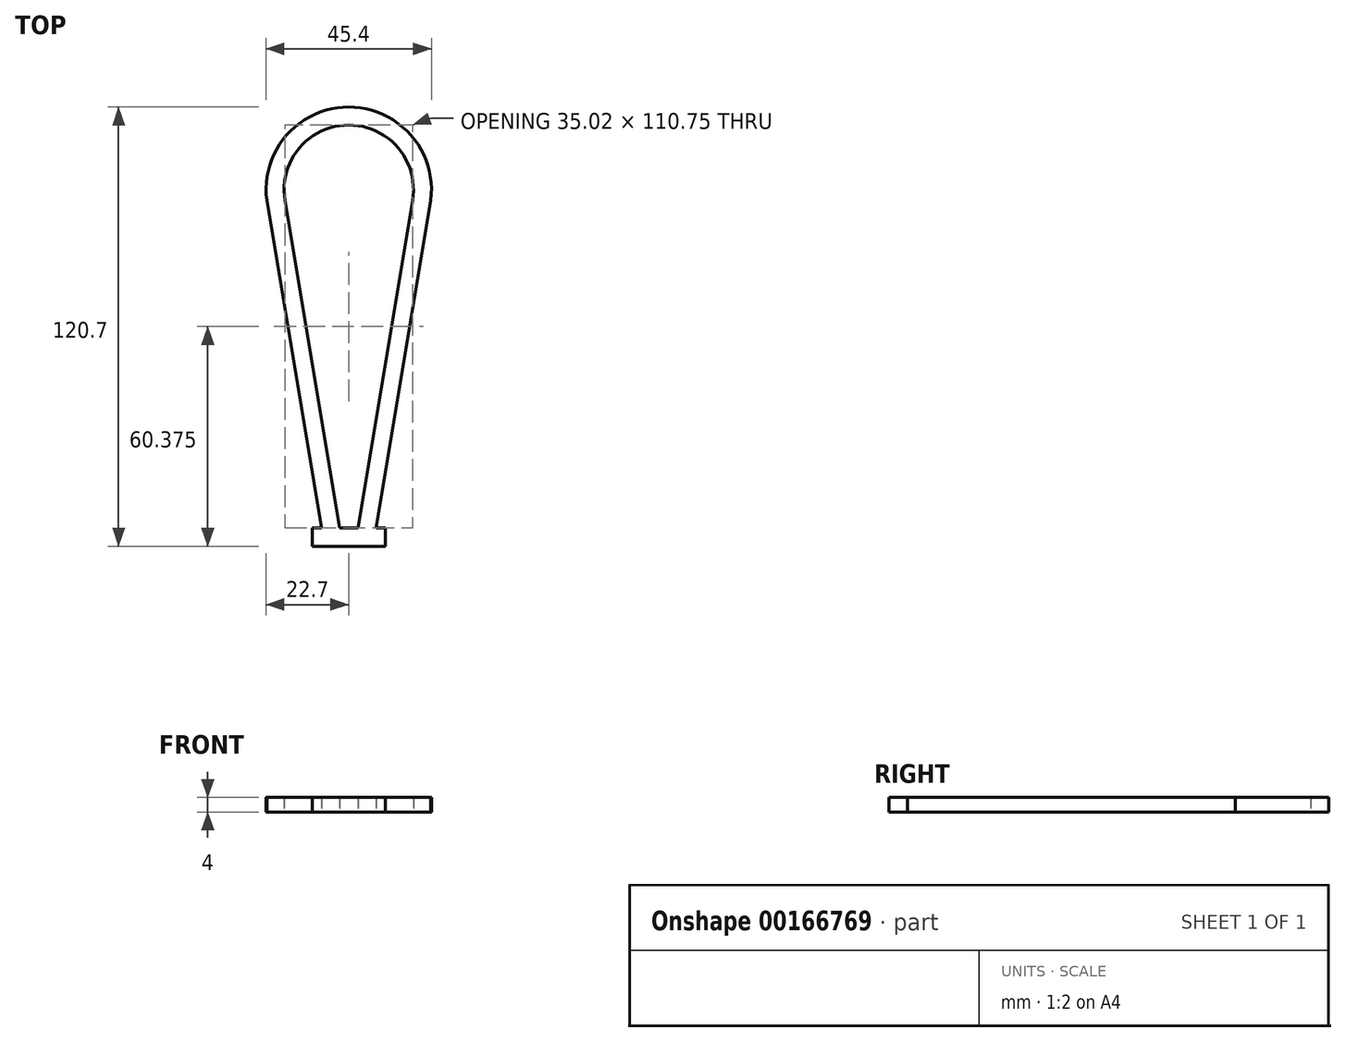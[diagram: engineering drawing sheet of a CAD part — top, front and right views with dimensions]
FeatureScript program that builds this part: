
annotation { "Feature Type Name" : "Feature", "Feature Type Description" : "" }
export const myFeature = defineFeature(function(context is Context, id is Id, definition is map)
    precondition{}
    {
        {
            var Q0;
            Q0=qCreatedBy(makeId("Top.planeOp"),FACE);
            var sketch = newSketch(context, id + "F0", { "sketchPlane" : qUnion([Q0])});
            skPoint(sketch, "E0", {"position": v(0, 108) * mm});
            skArc(sketch, "E1", {"start": v(-17.5, 105.08) * mm, "mid": v(0, 125.75) * mm, "end": v(17.5, 105.08) * mm});
            skLineSegment(sketch, "E2.bottom", {"start": v(10, 15) * mm, "end": v(-10, 15) * mm});
            skLineSegment(sketch, "E2.top", {"start": v(10, 10) * mm, "end": v(-10, 10) * mm});
            skLineSegment(sketch, "E2.left", {"start": v(10, 15) * mm, "end": v(10, 10) * mm});
            skLineSegment(sketch, "E2.right", {"start": v(-10, 15) * mm, "end": v(-10, 10) * mm});
            skPoint(sketch, "E3", {"position": v(-2.5, 15) * mm});
            skPoint(sketch, "E4", {"position": v(2.5, 15) * mm});
            skPoint(sketch, "E4.positionSnap0", {"position": v(0, 15) * mm});
            skLineSegment(sketch, "E5", {"start": v(17.5, 105.08) * mm, "end": v(2.5, 15) * mm});
            skLineSegment(sketch, "E6", {"start": v(-17.5, 105.08) * mm, "end": v(-2.5, 15) * mm});
            skLineSegment(sketch, "E7", {"start": v(22.5, 105.08) * mm, "end": v(7.5, 15) * mm});
            skLineSegment(sketch, "E8", {"start": v(-22.5, 105.08) * mm, "end": v(-7.5, 15) * mm});
            skArc(sketch, "E9", {"start": v(-22.5, 105.08) * mm, "mid": v(0, 130.7) * mm, "end": v(22.5, 105.08) * mm});
            skLineSegment(sketch, "E10", {"start": v(-2.5, 15) * mm, "end": v(2.5, 15) * mm, "construction": true});
            skSolve(sketch);
        }
        {
            var Q0;
            Q0 = qSketchRegion(id + "F0", true);
            extrude(context, id + "F1", {"entities" : qUnion([Q0]), "depth" : 4 * mm});
        }
    });
